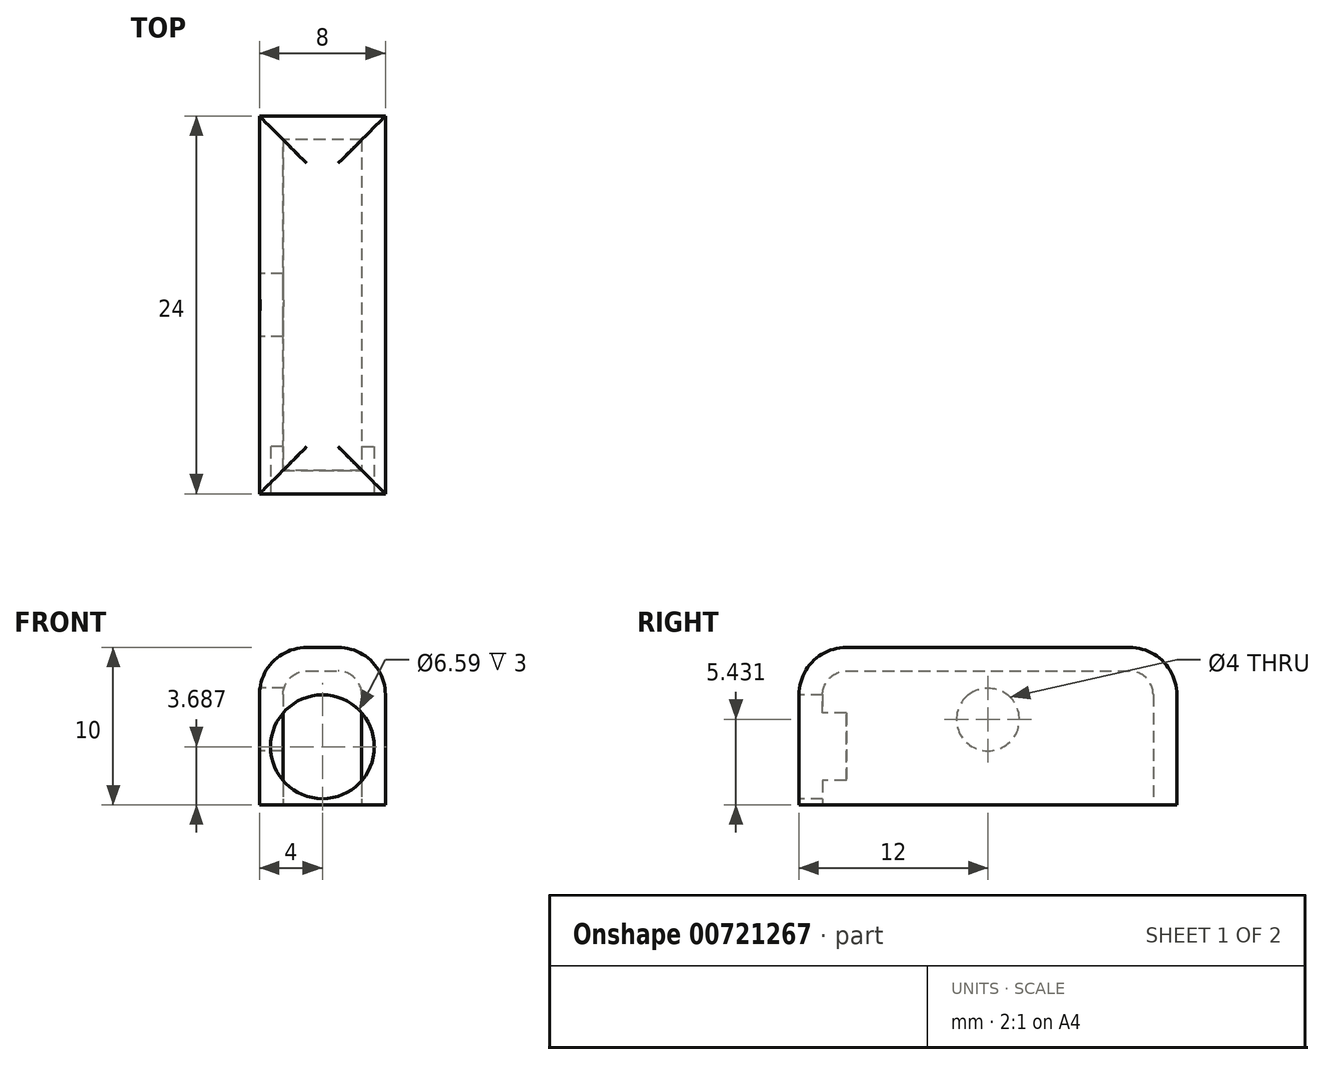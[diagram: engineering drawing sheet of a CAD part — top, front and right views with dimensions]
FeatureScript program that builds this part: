
annotation { "Feature Type Name" : "Feature", "Feature Type Description" : "" }
export const myFeature = defineFeature(function(context is Context, id is Id, definition is map)
    precondition{}
    {
        {
            var Q0;
            Q0=qCreatedBy(makeId("Top.planeOp"),FACE);
            var sketch = newSketch(context, id + "F0", { "sketchPlane" : qUnion([Q0])});
            skLineSegment(sketch, "E0.bottom", {"start": v(4, 12) * mm, "end": v(-4, 12) * mm});
            skLineSegment(sketch, "E0.top", {"start": v(4, -12) * mm, "end": v(-4, -12) * mm});
            skLineSegment(sketch, "E0.left", {"start": v(4, 12) * mm, "end": v(4, -12) * mm});
            skLineSegment(sketch, "E0.right", {"start": v(-4, 12) * mm, "end": v(-4, -12) * mm});
            skPoint(sketch, "E0.middle", {"position": v(0, 0) * mm});
            skSolve(sketch);
        }
        {
            var Q0;
            Q0=makeQuery(id+"F0.imprint","IMPRINT",FACE,{"disambiguationData":[TD([[makeQuery(id+"F0.imprint","IMPRINT",EDGE,{"derivedFrom":sQuery(id+"F0.wireOp",EDGE,"E0.bottom")}),1.0]])]});
            extrude(context, id + "F1", {"entities" : qUnion([Q0]), "depth" : 10 * mm, "offsetDistance" : 25.4 * mm});
        }
        {
            var Q0;
            Q0=makeQuery(id+"F1.opExtrude","CAP_FACE",FACE,{"disambiguationData":[OSD([sQuery(id+"F0.wireOp",EDGE,"E0.bottom"),sQuery(id+"F0.wireOp",EDGE,"E0.top"),sQuery(id+"F0.wireOp",EDGE,"E0.left"),sQuery(id+"F0.wireOp",EDGE,"E0.right")])],"isStart":false});
            fillet(context, id + "F2", {"entities" : qUnion([Q0]), "radius" : 3 * mm, "tangentPropagation" : true, "allowEdgeOverflow" : false});
        }
        {
            var Q0;
            Q0=makeQuery(id+"F1.opExtrude","SWEPT_FACE",FACE,{"disambiguationData":[OSD([sQuery(id+"F0.wireOp",EDGE,"E0.right")])]});
            var sketch = newSketch(context, id + "F3", { "sketchPlane" : qUnion([Q0])});
            skLineSegment(sketch, "E1", {"start": v(0, 7) * mm, "end": v(0, 0) * mm});
            skLineSegment(sketch, "E2", {"start": v(0, 0) * mm, "end": v(0, 3.5) * mm});
            skPoint(sketch, "E3", {"position": v(0, 3.5) * mm});
            skSolve(sketch);
        }
        {
            var Q0;
            Q0=makeQuery(id+"F1.opExtrude","CAP_FACE",FACE,{"disambiguationData":[OSD([sQuery(id+"F0.wireOp",EDGE,"E0.bottom"),sQuery(id+"F0.wireOp",EDGE,"E0.top"),sQuery(id+"F0.wireOp",EDGE,"E0.left"),sQuery(id+"F0.wireOp",EDGE,"E0.right")])],"isStart":true});
            shell(context, id + "F4", {"entities" : qUnion([Q0]), "thickness" : 1.5 * mm});
        }
        {
            var Q0;
            Q0=makeQuery(id+"F1.opExtrude","SWEPT_FACE",FACE,{"disambiguationData":[OSD([sQuery(id+"F0.wireOp",EDGE,"E0.top")])]});
            var sketch = newSketch(context, id + "F5", { "sketchPlane" : qUnion([Q0])});
            skPoint(sketch, "E4", {"position": v(0, 3.67) * mm});
            skSolve(sketch);
        }
        {
            var Q0;
            {var subQ0=sQuery(id+"F0.wireOp",EDGE,"E0.top");Q0=makeQuery(id+"F5.imprint","IMPRINT",FACE,{"disambiguationData":[TD([[makeQuery(id+"F5.imprint","IMPRINT",EDGE,{"derivedFrom":makeQuery(id+"F1.opExtrude","CAP_EDGE",EDGE,{"disambiguationData":[OSD([subQ0])],"isStart":true})}),-1.0]])]});}
            var sketch = newSketch(context, id + "F6", { "sketchPlane" : qUnion([Q0])});
            skCircle(sketch, "E5", {"center": v(0, 3.69) * mm, "radius": 3.3 * mm});
            skSolve(sketch);
        }
        {
            var Q0;
            Q0=makeQuery(id+"F6.imprint","IMPRINT",FACE,{"disambiguationData":[TD([[makeQuery(id+"F6.imprint","IMPRINT",EDGE,{"derivedFrom":sQuery(id+"F6.wireOp",EDGE,"E5")}),1.0]])]});
            extrude(context, id + "F7", {"entities" : qUnion([Q0]), "operationType" : NewBodyOperationType.REMOVE, "oppositeDirection" : true, "depth" : 3 * mm, "offsetDistance" : 25.4 * mm});
        }
        {
            var Q0;
            {var subQ4=sQuery(id+"F3.wireOp",EDGE,"E1");Q0=makeQuery(id+"F3.imprint","IMPRINT",FACE,{"disambiguationData":[TD([[makeQuery(id+"F3.imprint","IMPRINT",EDGE,{"derivedFrom":subQ4}),-1.0]])]});}
            var sketch = newSketch(context, id + "F8", { "sketchPlane" : qUnion([Q0])});
            skCircle(sketch, "E6", {"center": v(0, 5.43) * mm, "radius": 2 * mm});
            skSolve(sketch);
        }
        {
            var Q0;
            Q0 = qSketchRegion(id + "F8", true);
            extrude(context, id + "F9", {"entities" : qUnion([Q0]), "operationType" : NewBodyOperationType.REMOVE, "oppositeDirection" : true, "depth" : 3 * mm, "offsetDistance" : 25.4 * mm});
        }
    });
